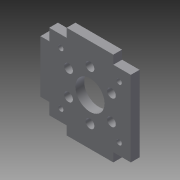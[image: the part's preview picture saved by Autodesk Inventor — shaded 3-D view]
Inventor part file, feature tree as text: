
AUTODESK INVENTOR PART (.ipt)
format: ipt  version: 2015 (Build 190159000, 159)  size: 158,208 bytes
history: native  units: mm
features: sketch x2, extrude x1, projected_geometry x1
ambient origin geometry x8: Origin, YZ Plane, XZ Plane, XY Plane, X Axis, Y Axis, Z Axis, Center Point
bodies: Solid1 (feature_tree)
feature tree (4):
  extrude  "Extrusion1"  Depth=22.0mm
  sketch  "Sketch3"  dims[d3=3.0mm d4=60.0mm d6=360.0deg d8=10.0mm d9=28.0mm d10=32.0mm d11=3.0mm d12=3.0mm d13=3.0mm d14=3.0mm d16=50.0mm d17=3.0mm d18=0.0mm d19=6.0mm d20=3.0mm d21=4.0mm d22=1.8mm d23=4.0mm d24=4.0mm d25=1.8mm d26=4.0mm d27=1.8mm d28=4.0mm d29=1.8mm]
  sketch  "Sketch1"  dims[d0=22.0mm d1=17.0mm]
  projected_geometry  "Projected Loop1"
